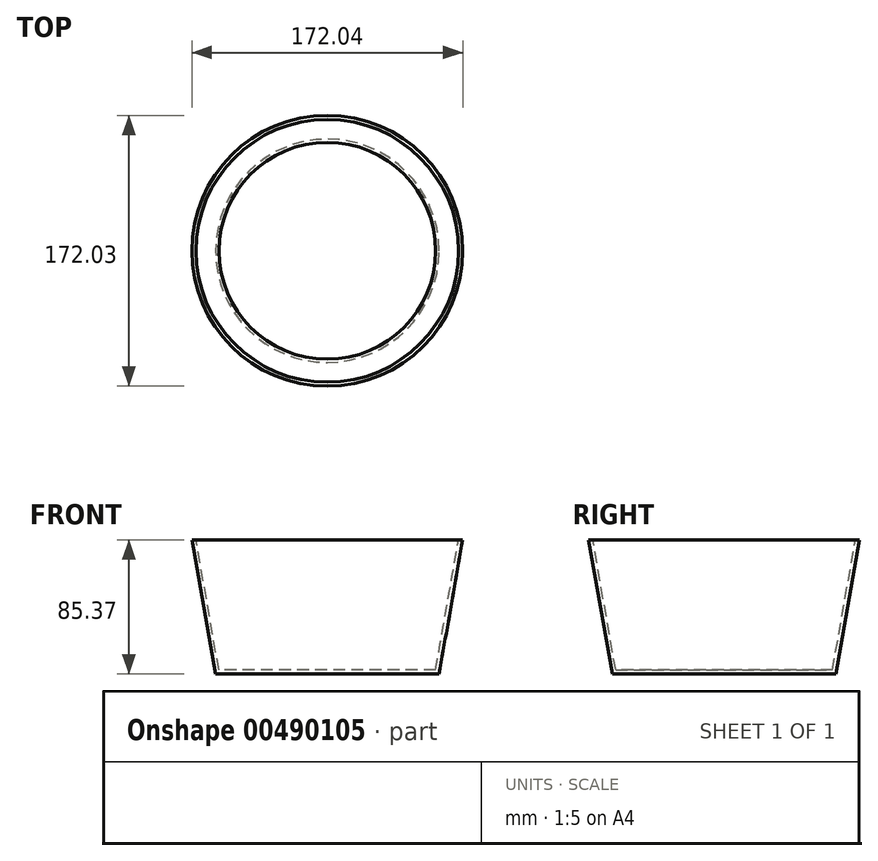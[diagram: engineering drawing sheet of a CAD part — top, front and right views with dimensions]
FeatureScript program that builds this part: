
annotation { "Feature Type Name" : "Feature", "Feature Type Description" : "" }
export const myFeature = defineFeature(function(context is Context, id is Id, definition is map)
    precondition{}
    {
        {
            var Q0;
            Q0=qCreatedBy(makeId("Top.planeOp"),FACE);
            var sketch = newSketch(context, id + "F0", { "sketchPlane" : qUnion([Q0])});
            skCircle(sketch, "E0", {"center": v(34.4, 0) * mm, "radius": 41.2 * mm});
            skCircle(sketch, "E1", {"center": v(-26.35, -54.18) * mm, "radius": 41.78 * mm});
            skCircle(sketch, "E2", {"center": v(-58.16, 94.14) * mm, "radius": 70.96 * mm});
            skCircle(sketch, "E3", {"center": v(100.69, -159.13) * mm, "radius": 51.54 * mm});
            skCircle(sketch, "E4", {"center": v(128.48, -11.77) * mm, "radius": 115.99 * mm});
            skSolve(sketch);
        }
        {
            var Q0;
            Q0=makeQuery(id+"F0.imprint","IMPRINT",FACE,{"disambiguationData":[TD([[makeQuery(id+"F0.imprint","IMPRINT",EDGE,{"derivedFrom":sQuery(id+"F0.wireOp",EDGE,"E2")}),1.0]])]});
            extrude(context, id + "F1", {"entities" : qUnion([Q0]), "depth" : 85.37 * mm, "hasDraft" : true, "draftAngle" : 10 * degree});
        }
        {
            var Q0;
            Q0=makeQuery(id+"F1.opExtrude","CAP_FACE",FACE,{"disambiguationData":[OSD([sQuery(id+"F0.wireOp",EDGE,"E2")])],"isStart":false});
            shell(context, id + "F2", {"entities" : qUnion([Q0]), "thickness" : 2.54 * mm});
        }
    });
